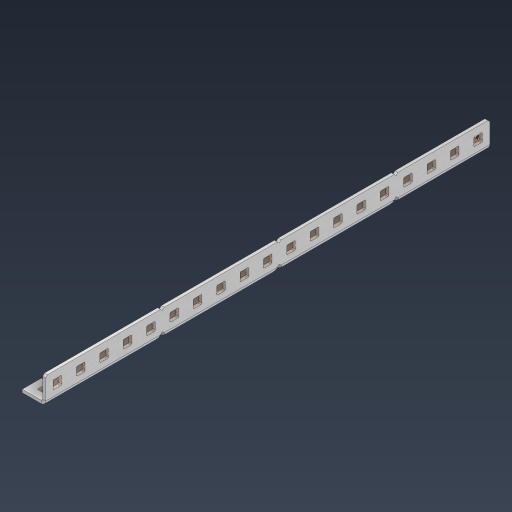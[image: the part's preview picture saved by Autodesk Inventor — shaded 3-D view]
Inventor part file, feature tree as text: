
AUTODESK INVENTOR PART (.ipt)
format: ipt  version: 2024.3 (Build 283343000, 343)  size: 828,928 bytes
history: native  units: in
note: dims shown in document units (in); Inventor stores cm internally (conversion verified against a paired STEP export)
features: other x64, extrude x55, sheet_metal_op x11, pattern_linear x2, mirror x1, chamfer x1, sketch x1
ambient origin geometry x8: Origin, YZ Plane, XZ Plane, XY Plane, X Axis, Y Axis, Z Axis, Center Point
bodies: Solid1 (feature_tree), Body (feature_tree)
feature tree (135):
  sheet_metal_op  "Flanges"
  other  "Flange Pattern Plane"
  other  "Flange Pattern Sketch"
  sheet_metal_op  "Flange Pattern"
  sheet_metal_op  "Body Pattern"
  pattern_linear  "Center Pattern"  Spacing1=9.5in  [1 undecoded]
  other  "Arc Length"
  mirror  "Notch Mirror"
  pattern_linear  "Notch Pattern"  Spacing1=0.0625in  [1 undecoded]
  chamfer  "End Chamfer"
  extrude  "Half Cut"  Depth=0.0625in
  other  "Plate1"
  sketch  "Sketch2"  dims[d0=1.0in d1=9.5in d2=0.0625in d3=0.0625in d4=0.0312in d5=0.125in d6=0.0625in d7=0.5in d8=90.0deg d9=0.0312in d10=0.25in d11=0.0625in d12=0.0625in d16=0.182in d17=0.02in d18=0.0625in d19=0.0in d20=0.25in d21=0.25in d38=7.4803in d40=0.5in d41=0.3937in d43=1.0in d46=0.172in d47=1.0in d48=0.0in d49=0.182in d50=0.02in d51=0.25in d52=0.25in d53=0.0625in d54=0.0in d55=0.172in d56=1.0in d57=0.0in d58=0.25in d60=7.4803in d62=0.5in d63=0.3937in d65=0.5in d85=0.1473in d86=0.1782in d88=0.04in d89=0.0625in d90=0.0in d91=0.04in d92=0.0491in d95=2.5in d96=0.04in d97=0.25in d98=45.0deg d99=0.25in d100=0.5in d101=0.0in d102=2.497in d106=0.182in d107=0.02in d108=0.5in d109=0.5in d110=0.0625in d111=0.0in d112=0.172in d113=0.5in d114=0.0in d117=0.5in d118=0.5in d119=0.5in]
  other  "Plate2"
  sheet_metal_op  "Bend1"
  sheet_metal_op  "Corner1"
  other  "Srf1"
  other  "Srf2"
  other  "Srf91"
  sheet_metal_op  "Body Pattern Sketch"
  other  "Srf92"
  other  "Srf786"
  other  "Srf823"
  other  "Srf824"
  other  "Srf825"
  other  "Srf826"
  other  "Srf827"
  other  "Srf828"
  other  "Srf829"
  other  "Srf856"
  other  "Srf857"
  other  "Srf858"
  other  "Srf859"
  other  "Srf860"
  other  "Srf861"
  other  "Srf862"
  other  "Srf889"
  other  "Srf890"
  other  "Srf891"
  other  "Srf892"
  other  "Srf893"
  other  "Srf894"
  other  "Srf895"
  other  "Srf896"
  other  "Srf922"
  other  "Srf923"
  other  "Srf924"
  other  "Srf925"
  other  "Srf926"
  other  "Srf959"
  other  "Srf960"
  other  "Srf961"
  other  "Srf962"
  other  "Srf963"
  other  "Srf996"
  other  "Srf997"
  other  "Srf998"
  other  "Srf999"
  other  "Srf1000"
  other  "Srf1143"
  other  "Srf1144"
  other  "Srf1145"
  other  "Srf1146"
  other  "Srf1147"
  other  "Srf1199"
  other  "Srf1200"
  other  "Srf1201"
  other  "Srf1202"
  other  "Srf1203"
  other  "Srf1255"
  other  "Srf1256"
  other  "Srf1257"
  other  "Srf1258"
  other  "Srf1259"
  sheet_metal_op  "Flange Stamp"
  sheet_metal_op  "Flange Circle"
  sheet_metal_op  "Body Stamp"
  sheet_metal_op  "Body Circle"
  other  "Center Stamp"
  other  "Center Circle"
  sheet_metal_op  "Notch"
  extrude  "ExtrusionSrf2"  Depth=0.0312in
  extrude  "ExtrusionSrf92"  Depth=0.5in
  extrude  "ExtrusionSrf823"  Depth=0.0625in
  extrude  "ExtrusionSrf824"  Depth=0.5in TaperAngle=90.0deg
  extrude  "ExtrusionSrf825"  Depth=0.5in
  extrude  "ExtrusionSrf826"  Depth=0.0625in
  extrude  "ExtrusionSrf827"  Depth=0.0625in
  extrude  "ExtrusionSrf828"  Depth=0.182in
  extrude  "ExtrusionSrf829"  Depth=0.02in
  extrude  "ExtrusionSrf856"  Depth=0.0625in
  extrude  "ExtrusionSrf857"  TaperAngle=0.0deg  [1 undecoded]
  extrude  "ExtrusionSrf858"  Depth=0.5in
  extrude  "ExtrusionSrf859"  Depth=0.5in
  extrude  "ExtrusionSrf860"  Depth=0.5in
  extrude  "ExtrusionSrf861"  Depth=0.5in
  extrude  "ExtrusionSrf862"  Depth=1.0in TaperAngle=0.0deg
  extrude  "ExtrusionSrf889"  Depth=0.182in
  extrude  "ExtrusionSrf890"  Depth=0.02in
  extrude  "ExtrusionSrf891"  Depth=0.5in
  extrude  "ExtrusionSrf892"  Depth=0.5in
  extrude  "ExtrusionSrf893"  Depth=0.0625in
  extrude  "ExtrusionSrf894"  TaperAngle=0.0deg  [1 undecoded]
  extrude  "ExtrusionSrf895"  Depth=0.5in
  extrude  "ExtrusionSrf896"  Depth=1.0in TaperAngle=0.0deg
  extrude  "ExtrusionSrf922"  Depth=0.5in
  extrude  "ExtrusionSrf923"  Depth=0.5in
  extrude  "ExtrusionSrf924"  Depth=0.5in
  extrude  "ExtrusionSrf925"  Depth=0.5in
  extrude  "ExtrusionSrf926"  Depth=0.5in
  extrude  "ExtrusionSrf959"  Depth=0.5in
  extrude  "ExtrusionSrf960"  Depth=0.0625in
  extrude  "ExtrusionSrf961"  TaperAngle=0.0deg  [1 undecoded]
  extrude  "ExtrusionSrf962"  Depth=0.5in
  extrude  "ExtrusionSrf963"  Depth=0.5in
  extrude  "ExtrusionSrf996"  Depth=0.5in
  extrude  "ExtrusionSrf997"  Depth=0.5in TaperAngle=45.0deg
  extrude  "ExtrusionSrf998"  Depth=0.5in
  extrude  "ExtrusionSrf999"  Depth=0.5in TaperAngle=0.0deg
  extrude  "ExtrusionSrf1000"  Depth=0.5in
  extrude  "ExtrusionSrf1143"  Depth=0.182in
  extrude  "ExtrusionSrf1144"  Depth=0.02in
  extrude  "ExtrusionSrf1145"  Depth=0.5in
  extrude  "ExtrusionSrf1146"  Depth=0.5in
  extrude  "ExtrusionSrf1147"  Depth=0.0625in
  extrude  "ExtrusionSrf1199"  TaperAngle=0.0deg  [1 undecoded]
  extrude  "ExtrusionSrf1200"  Depth=0.5in
  extrude  "ExtrusionSrf1201"  Depth=0.5in TaperAngle=0.0deg
  extrude  "ExtrusionSrf1202"  Depth=0.5in
  extrude  "ExtrusionSrf1203"  Depth=0.5in
  extrude  "ExtrusionSrf1255"  Depth=0.5in
  extrude  "ExtrusionSrf1256"  [1 undecoded]
  extrude  "ExtrusionSrf1257"  [1 undecoded]
  extrude  "ExtrusionSrf1258"  [1 undecoded]
  extrude  "ExtrusionSrf1259"  [1 undecoded]
note: 10 required parameter values undecoded (feature->parameter linkage not recoverable at this tier; creation-order binding heuristic only, values carry confidence <= 0.55)
